# Revit family: Safehook_Linc
name_source: partatom
category: Specialty Equipment
units: mm (PartAtom-declared; Revit-internal decimal feet)

## family parameters
Cut with Voids When Loaded = No
Host = Face
Part Type = Normal
Room Calculation Point = No
Round Connector Dimension = Use Diameter
Shared = No

## types (4) — shared parameters
Manufacturer = Linc Furniture
Revision = 20230624
URL = https://lincfurniture.com.au
zero-valued in all types: Default Elevation

## per-type parameters (varying)
| type | ButtonType | HideOZYhook | HookType | ShowOZYhook |
| Euro V2 Bag Hook | Safehook_Button : Large | Yes | Safehook_Body_EuroIhookOZIhook : Euro V2 Bag Hook and Ihook Mk2 Bag Hook | No |
| Ihook Mk2 Bag Hook | Safehook_Button : Small | Yes | Safehook_Body_EuroIhookOZIhook : Euro V2 Bag Hook and Ihook Mk2 Bag Hook | No |
| OZIhook Bag Hook | Safehook_Button : Small | Yes | Safehook_Body_EuroIhookOZIhook : OZIhook Bag Hook | No |
| OZYhook Bag Hook | Safehook_Button : Small | No | Safehook_Body_OZYhook : Type 1 | Yes |

note: column(s) folded — value = type name in every type: Description, Type Comments

## geometry (parser evidence)
native form markers: Sweep x22
no freeform markers — native parametric forms only
